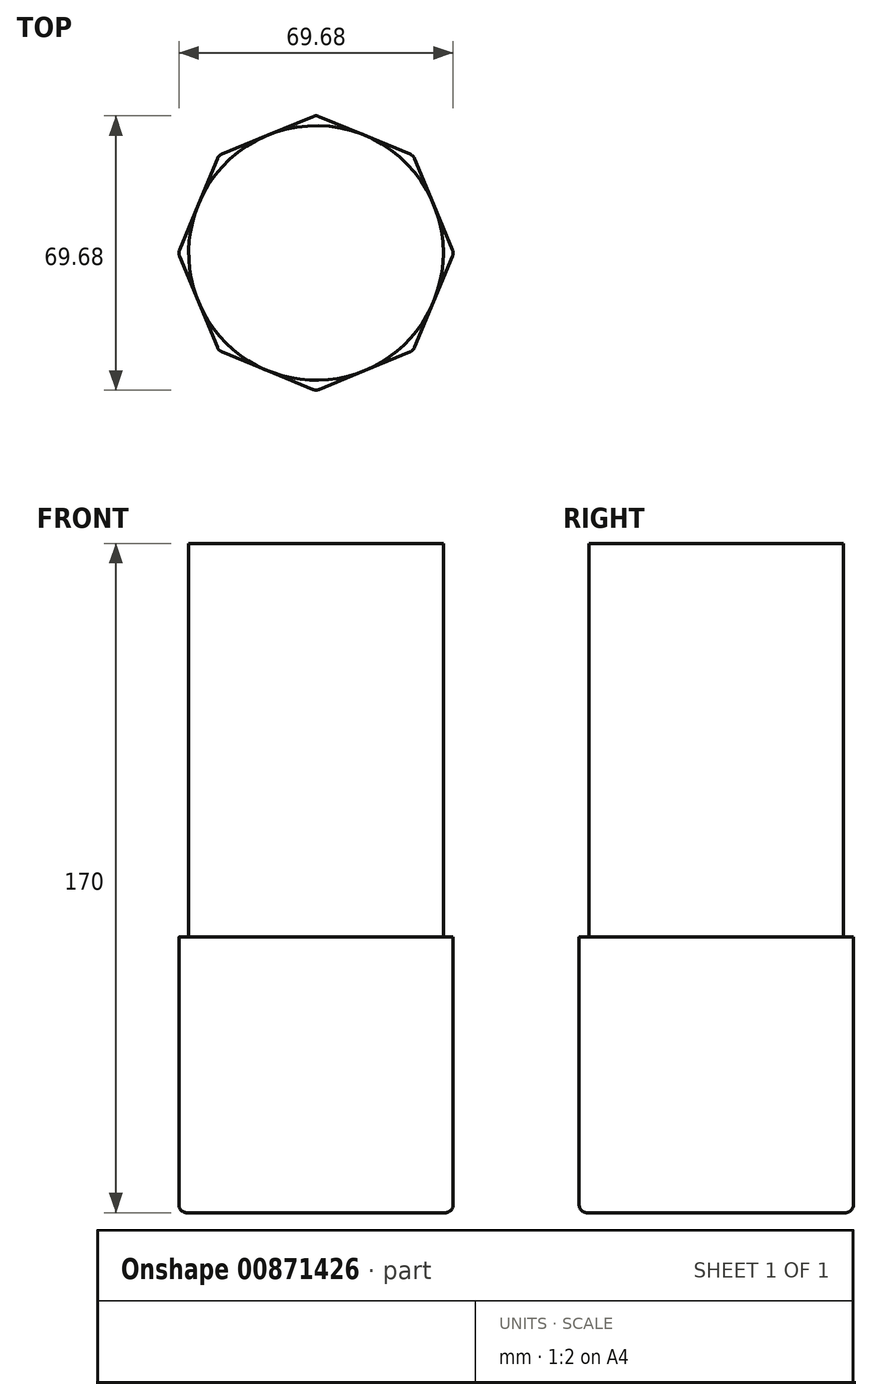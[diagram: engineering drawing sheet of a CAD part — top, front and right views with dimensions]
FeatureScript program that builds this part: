
annotation { "Feature Type Name" : "Feature", "Feature Type Description" : "" }
export const myFeature = defineFeature(function(context is Context, id is Id, definition is map)
    precondition{}
    {
        {
            var Q0;
            Q0=qCreatedBy(makeId("Top.planeOp"),FACE);
            var sketch = newSketch(context, id + "F0", { "sketchPlane" : qUnion([Q0])});
            skCircle(sketch, "E0.cCircle", {"center": v(0, 0) * mm, "radius": 35 * mm, "construction": true});
            skLineSegment(sketch, "E0.0", {"start": v(0, -35) * mm, "end": v(-24.75, -24.75) * mm});
            skLineSegment(sketch, "E0.1", {"start": v(-24.75, -24.75) * mm, "end": v(-35, 0) * mm});
            skLineSegment(sketch, "E0.2", {"start": v(-35, 0) * mm, "end": v(-24.75, 24.75) * mm});
            skLineSegment(sketch, "E0.3", {"start": v(-24.75, 24.75) * mm, "end": v(0, 35) * mm});
            skLineSegment(sketch, "E0.4", {"start": v(0, 35) * mm, "end": v(24.75, 24.75) * mm});
            skLineSegment(sketch, "E0.5", {"start": v(24.75, 24.75) * mm, "end": v(35, 0) * mm});
            skLineSegment(sketch, "E0.6", {"start": v(35, 0) * mm, "end": v(24.75, -24.75) * mm});
            skLineSegment(sketch, "E0.7", {"start": v(24.75, -24.75) * mm, "end": v(0, -35) * mm});
            skSolve(sketch);
        }
        {
            var Q0;
            Q0 = qSketchRegion(id + "F0", true);
            extrude(context, id + "F1", {"entities" : qUnion([Q0]), "depth" : 70 * mm, "offsetDistance" : 25 * mm});
        }
        {
            var Q0;
            Q0=makeQuery(id+"F1.opExtrude","SWEPT_EDGE",EDGE,{"disambiguationData":[OSD([sQuery(id+"F0.wireOp",EDGE,"E0.0"),sQuery(id+"F0.wireOp",EDGE,"E0.7")])]});
            var Q1;
            Q1=makeQuery(id+"F1.opExtrude","SWEPT_EDGE",EDGE,{"disambiguationData":[OSD([sQuery(id+"F0.wireOp",EDGE,"E0.0"),sQuery(id+"F0.wireOp",EDGE,"E0.1")])]});
            var Q2;
            Q2=makeQuery(id+"F1.opExtrude","SWEPT_EDGE",EDGE,{"disambiguationData":[OSD([sQuery(id+"F0.wireOp",EDGE,"E0.6"),sQuery(id+"F0.wireOp",EDGE,"E0.7")])]});
            var Q3;
            Q3=makeQuery(id+"F1.opExtrude","SWEPT_EDGE",EDGE,{"disambiguationData":[OSD([sQuery(id+"F0.wireOp",EDGE,"E0.5"),sQuery(id+"F0.wireOp",EDGE,"E0.6")])]});
            var Q4;
            Q4=makeQuery(id+"F1.opExtrude","SWEPT_EDGE",EDGE,{"disambiguationData":[OSD([sQuery(id+"F0.wireOp",EDGE,"E0.4"),sQuery(id+"F0.wireOp",EDGE,"E0.5")])]});
            var Q5;
            Q5=makeQuery(id+"F1.opExtrude","SWEPT_EDGE",EDGE,{"disambiguationData":[OSD([sQuery(id+"F0.wireOp",EDGE,"E0.3"),sQuery(id+"F0.wireOp",EDGE,"E0.4")])]});
            var Q6;
            Q6=makeQuery(id+"F1.opExtrude","SWEPT_EDGE",EDGE,{"disambiguationData":[OSD([sQuery(id+"F0.wireOp",EDGE,"E0.2"),sQuery(id+"F0.wireOp",EDGE,"E0.3")])]});
            var Q7;
            Q7=makeQuery(id+"F1.opExtrude","SWEPT_EDGE",EDGE,{"disambiguationData":[OSD([sQuery(id+"F0.wireOp",EDGE,"E0.1"),sQuery(id+"F0.wireOp",EDGE,"E0.2")])]});
            var Q8;
            Q8=makeQuery(id+"F1.opExtrude","CAP_FACE",FACE,{"disambiguationData":[OSD([sQuery(id+"F0.wireOp",EDGE,"E0.0"),sQuery(id+"F0.wireOp",EDGE,"E0.1"),sQuery(id+"F0.wireOp",EDGE,"E0.2"),sQuery(id+"F0.wireOp",EDGE,"E0.3"),sQuery(id+"F0.wireOp",EDGE,"E0.4"),sQuery(id+"F0.wireOp",EDGE,"E0.5"),sQuery(id+"F0.wireOp",EDGE,"E0.6"),sQuery(id+"F0.wireOp",EDGE,"E0.7")])],"isStart":true});
            fillet(context, id + "F2", {"entities" : qUnion([Q0, Q1, Q2, Q3, Q4, Q5, Q6, Q7, Q8]), "radius" : 2 * mm, "tangentPropagation" : true, "allowEdgeOverflow" : false});
        }
        {
            var Q0;
            Q0=makeQuery(id+"F1.opExtrude","CAP_FACE",FACE,{"disambiguationData":[OSD([sQuery(id+"F0.wireOp",EDGE,"E0.0"),sQuery(id+"F0.wireOp",EDGE,"E0.1"),sQuery(id+"F0.wireOp",EDGE,"E0.2"),sQuery(id+"F0.wireOp",EDGE,"E0.3"),sQuery(id+"F0.wireOp",EDGE,"E0.4"),sQuery(id+"F0.wireOp",EDGE,"E0.5"),sQuery(id+"F0.wireOp",EDGE,"E0.6"),sQuery(id+"F0.wireOp",EDGE,"E0.7")])],"isStart":false});
            var sketch = newSketch(context, id + "F3", { "sketchPlane" : qUnion([Q0])});
            skCircle(sketch, "E1", {"center": v(0, 0) * mm, "radius": 32.34 * mm});
            skSolve(sketch);
        }
        {
            var Q0;
            {var subQ0=sQuery(id+"F3.wireOp",EDGE,"E1");var subQ4=makeQuery(id+"F3.imprint","INTERSECT",VERTEX,{"derivedFrom":[makeQuery(id+"F1.opExtrude","CAP_EDGE",EDGE,{"disambiguationData":[OSD([sQuery(id+"F0.wireOp",EDGE,"E0.4")])],"isStart":false}),subQ0]});Q0=makeQuery(id+"F3.imprint","IMPRINT",FACE,{"disambiguationData":[TD([[makeQuery(id+"F3.imprint","IMPRINT",EDGE,{"disambiguationData":[TD([[subQ4,1.0]])],"derivedFrom":subQ0}),1.0]])]});}
            extrude(context, id + "F4", {"entities" : qUnion([Q0]), "operationType" : NewBodyOperationType.ADD, "depth" : 100 * mm, "offsetDistance" : 25 * mm});
        }
    });
